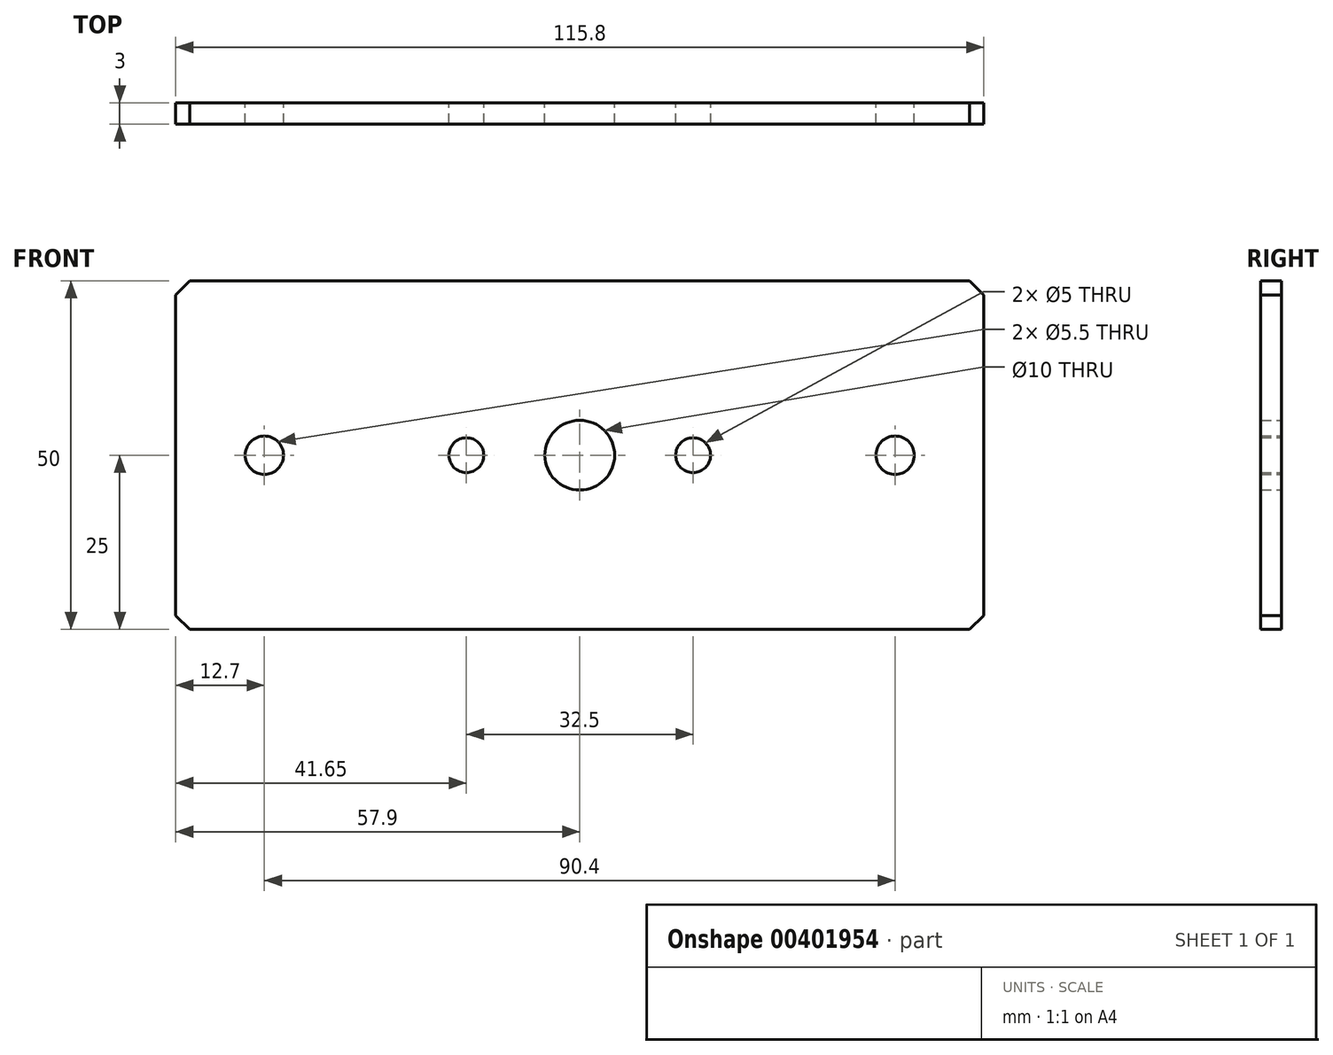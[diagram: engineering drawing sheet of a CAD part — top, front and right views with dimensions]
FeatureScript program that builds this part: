
annotation { "Feature Type Name" : "Feature", "Feature Type Description" : "" }
export const myFeature = defineFeature(function(context is Context, id is Id, definition is map)
    precondition{}
    {
        {
            var Q0;
            Q0=qCreatedBy(makeId("Front.planeOp"),FACE);
            var sketch = newSketch(context, id + "F0", { "sketchPlane" : qUnion([Q0])});
            skLineSegment(sketch, "E0.bottom", {"start": v(0, 0) * mm, "end": v(115.8, 0) * mm});
            skLineSegment(sketch, "E0.top", {"start": v(0, 50) * mm, "end": v(115.8, 50) * mm});
            skLineSegment(sketch, "E0.left", {"start": v(0, 0) * mm, "end": v(0, 50) * mm});
            skLineSegment(sketch, "E0.right", {"start": v(115.8, 0) * mm, "end": v(115.8, 50) * mm});
            skLineSegment(sketch, "E1", {"start": v(25.4, 50) * mm, "end": v(25.4, 0) * mm, "construction": true});
            skLineSegment(sketch, "E2", {"start": v(90.4, 50) * mm, "end": v(90.4, 0) * mm, "construction": true});
            skLineSegment(sketch, "E3", {"start": v(0, 25) * mm, "end": v(25.4, 25) * mm, "construction": true});
            skLineSegment(sketch, "E4", {"start": v(90.4, 25) * mm, "end": v(115.8, 25) * mm, "construction": true});
            skCircle(sketch, "E5", {"center": v(12.7, 25) * mm, "radius": 2.75 * mm});
            skCircle(sketch, "E6", {"center": v(103.1, 25) * mm, "radius": 2.75 * mm});
            skLineSegment(sketch, "E7", {"start": v(25.4, 25) * mm, "end": v(57.9, 25) * mm, "construction": true});
            skLineSegment(sketch, "E8", {"start": v(57.9, 25) * mm, "end": v(90.4, 25) * mm, "construction": true});
            skCircle(sketch, "E9", {"center": v(41.65, 25) * mm, "radius": 2.5 * mm});
            skCircle(sketch, "E10", {"center": v(74.15, 25) * mm, "radius": 2.5 * mm});
            skCircle(sketch, "E11", {"center": v(57.9, 25) * mm, "radius": 5 * mm});
            skSolve(sketch);
        }
        {
            var Q0;
            Q0 = qSketchRegion(id + "F0", true);
            extrude(context, id + "F1", {"entities" : qUnion([Q0]), "depth" : 3 * mm});
        }
        {
            var Q0;
            Q0=makeQuery(id+"F1.opExtrude","SWEPT_EDGE",EDGE,{"disambiguationData":[OSD([sQuery(id+"F0.wireOp",EDGE,"E0.bottom"),sQuery(id+"F0.wireOp",EDGE,"E0.left")])]});
            var Q1;
            Q1=makeQuery(id+"F1.opExtrude","SWEPT_EDGE",EDGE,{"disambiguationData":[OSD([sQuery(id+"F0.wireOp",EDGE,"E0.top"),sQuery(id+"F0.wireOp",EDGE,"E0.left")])]});
            var Q2;
            Q2=makeQuery(id+"F1.opExtrude","SWEPT_EDGE",EDGE,{"disambiguationData":[OSD([sQuery(id+"F0.wireOp",EDGE,"E0.bottom"),sQuery(id+"F0.wireOp",EDGE,"E0.right")])]});
            var Q3;
            Q3=makeQuery(id+"F1.opExtrude","SWEPT_EDGE",EDGE,{"disambiguationData":[OSD([sQuery(id+"F0.wireOp",EDGE,"E0.top"),sQuery(id+"F0.wireOp",EDGE,"E0.right")])]});
            chamfer(context, id + "F2", {"entities" : qUnion([Q0, Q1, Q2, Q3]), "width" : 2 * mm, "tangentPropagation" : true});
        }
    });
